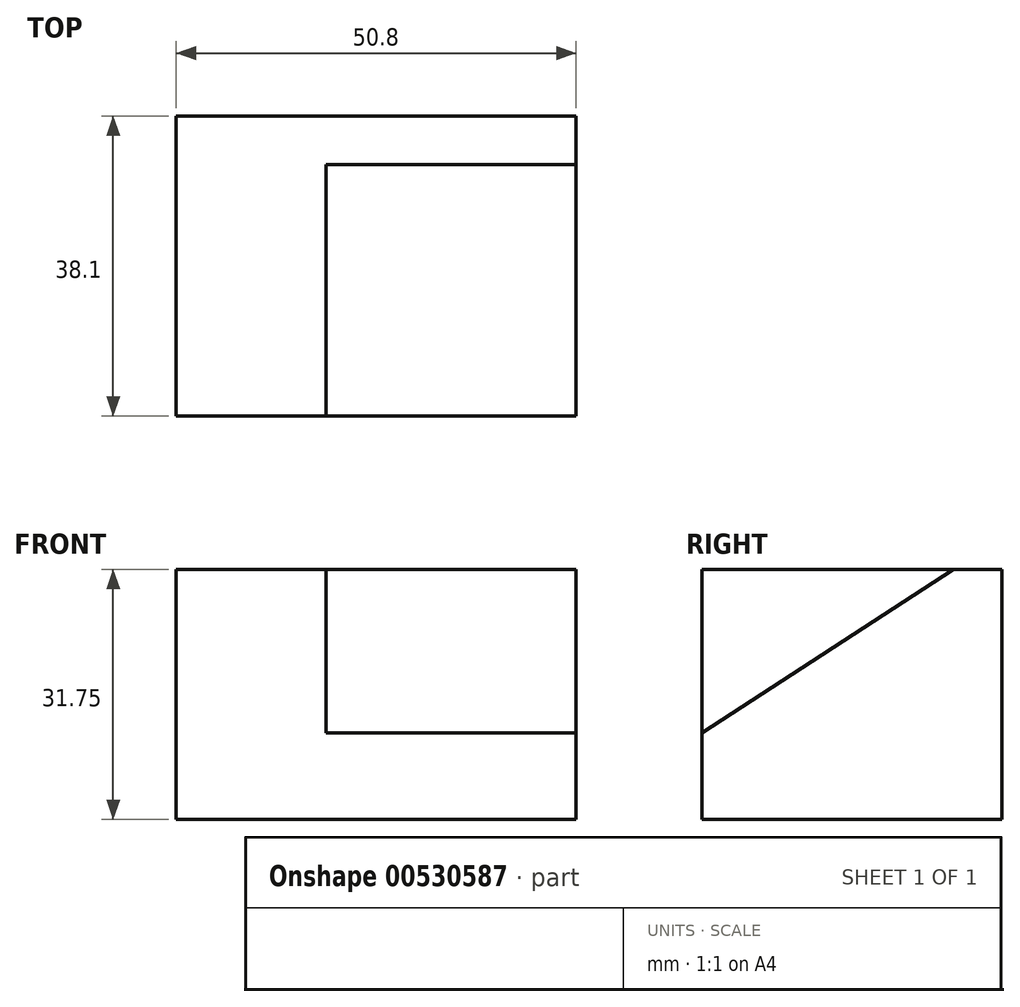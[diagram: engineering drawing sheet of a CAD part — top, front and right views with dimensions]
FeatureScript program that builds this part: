
annotation { "Feature Type Name" : "Feature", "Feature Type Description" : "" }
export const myFeature = defineFeature(function(context is Context, id is Id, definition is map)
    precondition{}
    {
        {
            var Q0;
            Q0=qCreatedBy(makeId("Right.planeOp"),FACE);
            var sketch = newSketch(context, id + "F0", { "sketchPlane" : qUnion([Q0])});
            skLineSegment(sketch, "E0", {"start": v(-62.45, 35.2) * mm, "end": v(-24.35, 35.2) * mm});
            skLineSegment(sketch, "E1", {"start": v(-24.35, 35.2) * mm, "end": v(-24.35, 3.44) * mm});
            skLineSegment(sketch, "E2", {"start": v(-24.35, 3.44) * mm, "end": v(-62.45, 3.44) * mm});
            skLineSegment(sketch, "E3", {"start": v(-62.45, 3.44) * mm, "end": v(-62.45, 35.2) * mm});
            skSolve(sketch);
        }
        {
            var Q0;
            Q0 = qSketchRegion(id + "F0", true);
            extrude(context, id + "F1", {"entities" : qUnion([Q0]), "depth" : 25.4 * mm, "offsetDistance" : 25.4 * mm});
        }
        {
            var Q0;
            Q0=makeQuery(id+"F1.opExtrude","CAP_FACE",FACE,{"disambiguationData":[OSD([sQuery(id+"F0.wireOp",EDGE,"E0"),sQuery(id+"F0.wireOp",EDGE,"E1"),sQuery(id+"F0.wireOp",EDGE,"E2"),sQuery(id+"F0.wireOp",EDGE,"E3")])],"isStart":false});
            var sketch = newSketch(context, id + "F2", { "sketchPlane" : qUnion([Q0])});
            skLineSegment(sketch, "E4", {"start": v(-30.5, 35.2) * mm, "end": v(-62.45, 14.44) * mm});
            skSolve(sketch);
        }
        {
            var Q0;
            {var subQ2=sQuery(id+"F2.wireOp",EDGE,"E4");Q0=makeQuery(id+"F2.imprint","IMPRINT",FACE,{"disambiguationData":[TD([[makeQuery(id+"F2.imprint","IMPRINT",EDGE,{"derivedFrom":subQ2}),1.0]])]});}
            extrude(context, id + "F3", {"entities" : qUnion([Q0]), "operationType" : NewBodyOperationType.ADD, "depth" : 25.4 * mm, "offsetDistance" : 25.4 * mm});
        }
        {
            var Q0;
            Q0=makeQuery(id+"F1.opExtrude","CAP_FACE",FACE,{"disambiguationData":[OSD([sQuery(id+"F0.wireOp",EDGE,"E0"),sQuery(id+"F0.wireOp",EDGE,"E1"),sQuery(id+"F0.wireOp",EDGE,"E2"),sQuery(id+"F0.wireOp",EDGE,"E3")])],"isStart":false});
            extrude(context, id + "F4", {"entities" : qUnion([Q0]), "operationType" : NewBodyOperationType.REMOVE, "oppositeDirection" : true, "depth" : 6.35 * mm, "offsetDistance" : 25.4 * mm});
        }
    });
